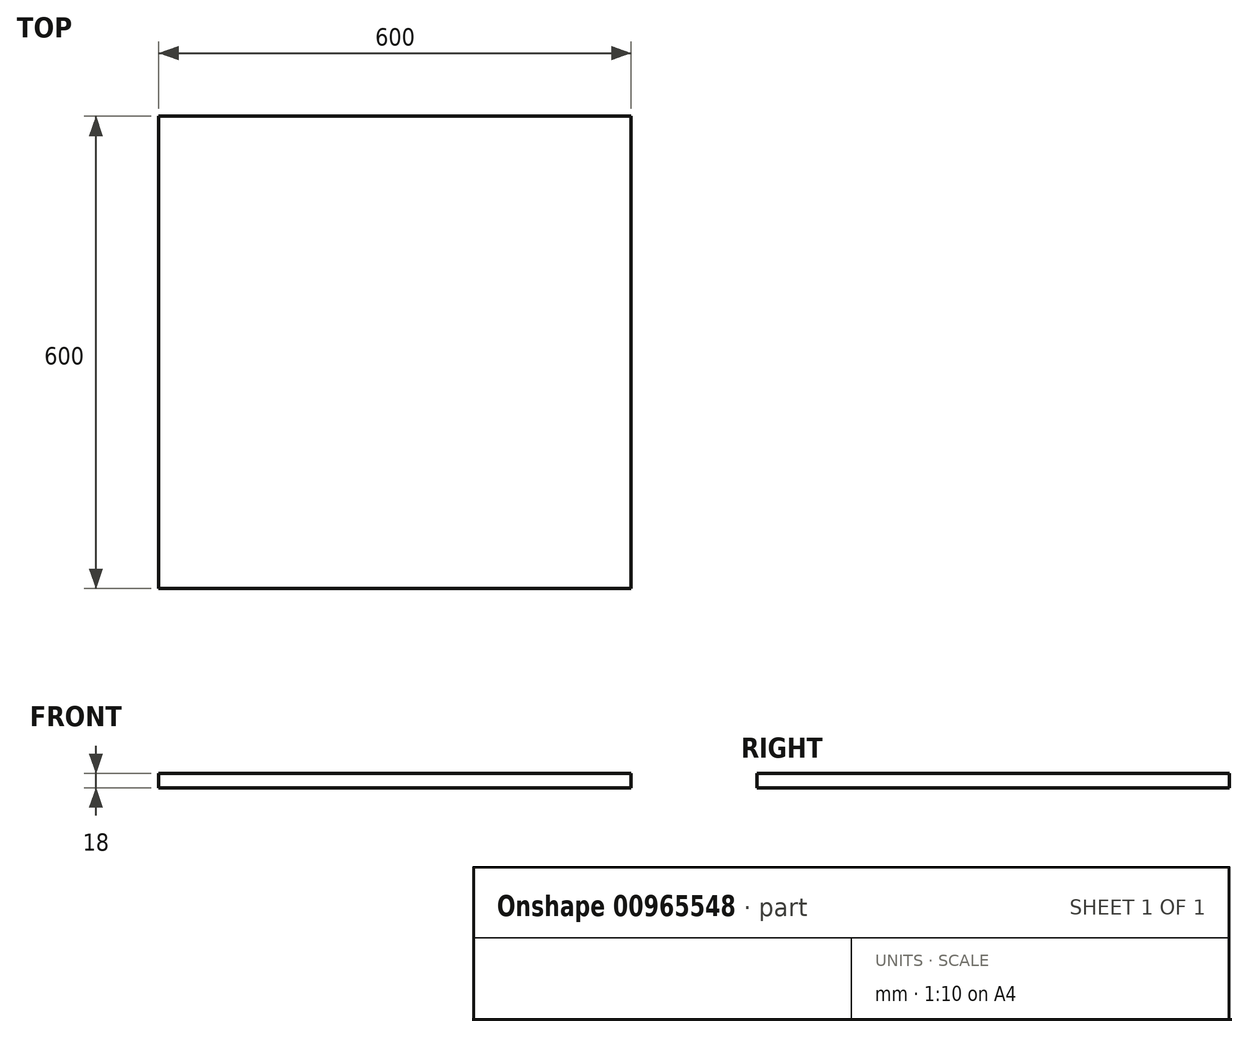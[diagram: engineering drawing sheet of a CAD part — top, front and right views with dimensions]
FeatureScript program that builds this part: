
annotation { "Feature Type Name" : "Feature", "Feature Type Description" : "" }
export const myFeature = defineFeature(function(context is Context, id is Id, definition is map)
    precondition{}
    {
        {
            var Q0;
            Q0=qCreatedBy(makeId("Top.planeOp"),FACE);
            var sketch = newSketch(context, id + "F0", { "sketchPlane" : qUnion([Q0])});
            skLineSegment(sketch, "E0.bottom", {"start": v(300, 300) * mm, "end": v(-300, 300) * mm});
            skLineSegment(sketch, "E0.top", {"start": v(300, -300) * mm, "end": v(-300, -300) * mm});
            skLineSegment(sketch, "E0.left", {"start": v(300, 300) * mm, "end": v(300, -300) * mm});
            skLineSegment(sketch, "E0.right", {"start": v(-300, 300) * mm, "end": v(-300, -300) * mm});
            skPoint(sketch, "E0.middle", {"position": v(0, 0) * mm});
            skSolve(sketch);
        }
        {
            var Q0;
            Q0=makeQuery(id+"F0.imprint","IMPRINT",FACE,{"disambiguationData":[TD([[makeQuery(id+"F0.imprint","IMPRINT",EDGE,{"derivedFrom":sQuery(id+"F0.wireOp",EDGE,"E0.bottom")}),1.0]])]});
            extrude(context, id + "F1", {"entities" : qUnion([Q0]), "depth" : 18 * mm, "offsetDistance" : 25 * mm});
        }
    });
